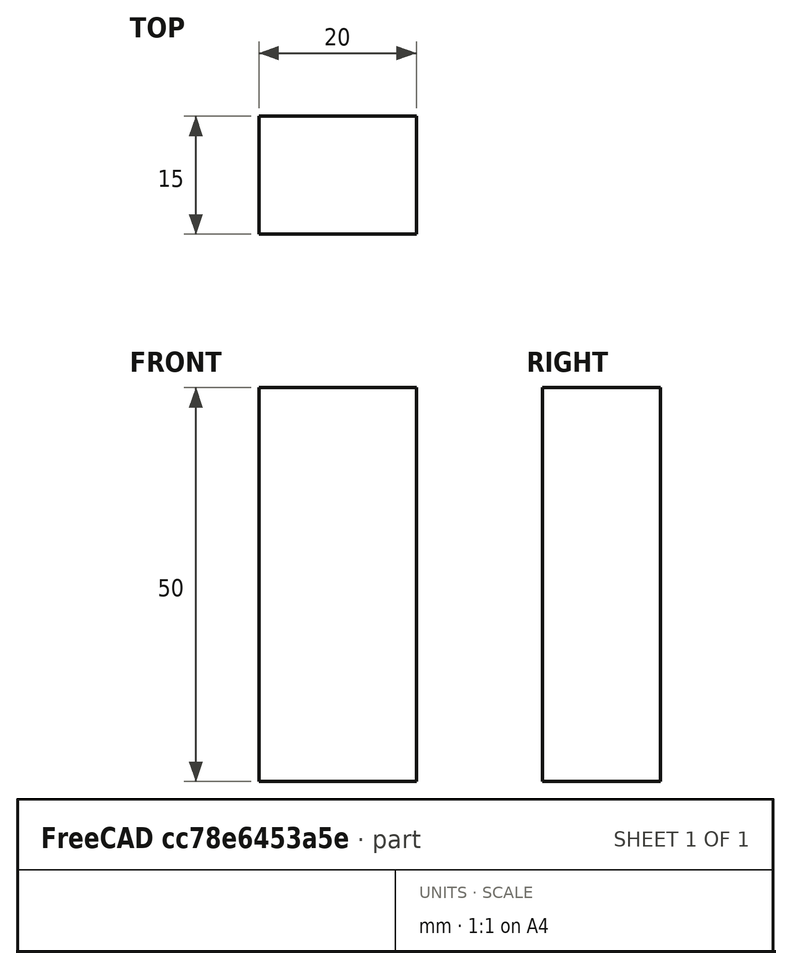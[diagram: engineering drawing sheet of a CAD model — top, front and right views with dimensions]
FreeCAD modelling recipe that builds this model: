
FCSTD DOCUMENT  (FreeCAD 0.15R4671 (Git))
Label: Flat Bar 20x15 EN10058 S235JR
License: All rights reserved
LicenseURL: http://en.wikipedia.org/wiki/All_rights_reserved
objects: Sketcher::SketchObject×1, Part::Extrusion×1
note: 2 computed .brp shape members not serialized (recipe doc carries the construction recipe); baked Part::Feature solids carry a one-line shape summary decoded from their .brp

FEATURE [Sketcher::SketchObject] Sketch
  sketch-geometry (4):
    g0: LineSegment StartX=-10 StartY=-7.5 StartZ=0 EndX=10 EndY=-7.5 EndZ=0
    g1: LineSegment StartX=10 StartY=-7.5 StartZ=0 EndX=10 EndY=7.5 EndZ=0
    g2: LineSegment StartX=10 StartY=7.5 StartZ=0 EndX=-10 EndY=7.5 EndZ=0
    g3: LineSegment StartX=-10 StartY=7.5 StartZ=0 EndX=-10 EndY=-7.5 EndZ=0
  constraints (12):
    c: Coincident(g0,g1)
    c: Coincident(g1,g2)
    c: Coincident(g2,g3)
    c: Coincident(g3,g0)
    c: Horizontal(g0)
    c: Horizontal(g2)
    c: Vertical(g1)
    c: Vertical(g3)
    c: Symmetric(g1,g2,g-2)
    c: Symmetric(g0,g1,g-1)
    c: DistanceY(g1) = 15
    c: DistanceX(g0) = 20
FEATURE [Part::Extrusion] Extrude  label="Flat Bar 20x15 EN10058 S235JR"
  Base = -> Sketch
  Dir = (0,0,50)
  Solid = true
